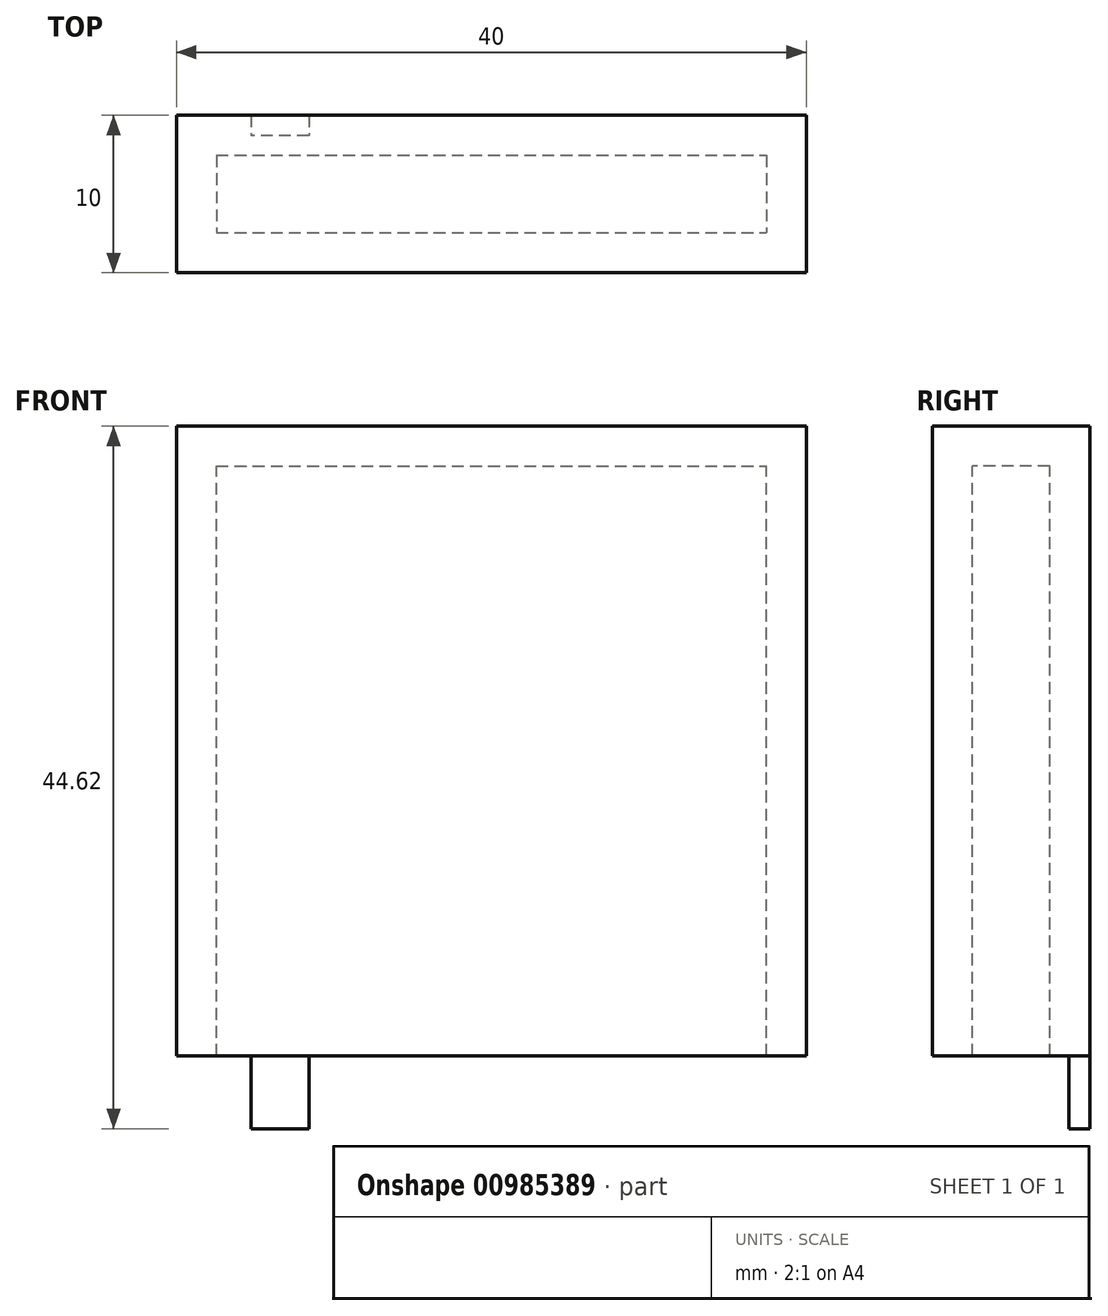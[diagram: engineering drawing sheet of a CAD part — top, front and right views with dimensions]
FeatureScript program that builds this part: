
annotation { "Feature Type Name" : "Feature", "Feature Type Description" : "" }
export const myFeature = defineFeature(function(context is Context, id is Id, definition is map)
    precondition{}
    {
        {
            var Q0;
            Q0=qCreatedBy(makeId("Front.planeOp"),FACE);
            var sketch = newSketch(context, id + "F0", { "sketchPlane" : qUnion([Q0])});
            skLineSegment(sketch, "E0.bottom", {"start": v(0, 0) * mm, "end": v(40, 0) * mm});
            skLineSegment(sketch, "E0.top", {"start": v(0, 40) * mm, "end": v(40, 40) * mm});
            skLineSegment(sketch, "E0.left", {"start": v(0, 0) * mm, "end": v(0, 40) * mm});
            skLineSegment(sketch, "E0.right", {"start": v(40, 0) * mm, "end": v(40, 40) * mm});
            skSolve(sketch);
        }
        {
            var Q0;
            Q0=makeQuery(id+"F0.imprint","IMPRINT",FACE,{"disambiguationData":[TD([[makeQuery(id+"F0.imprint","IMPRINT",EDGE,{"derivedFrom":sQuery(id+"F0.wireOp",EDGE,"E0.bottom")}),1.0]])]});
            extrude(context, id + "F1", {"entities" : qUnion([Q0]), "oppositeDirection" : true, "depth" : 10 * mm, "offsetDistance" : 25.4 * mm});
        }
        {
            var Q0;
            Q0=makeQuery(id+"F1.opExtrude","SWEPT_FACE",FACE,{"disambiguationData":[OSD([sQuery(id+"F0.wireOp",EDGE,"E0.bottom")])]});
            shell(context, id + "F2", {"entities" : qUnion([Q0]), "thickness" : 2.54 * mm});
        }
        {
            var Q0;
            Q0=makeQuery(id+"F1.opExtrude","SWEPT_FACE",FACE,{"disambiguationData":[OSD([sQuery(id+"F0.wireOp",EDGE,"E0.bottom")])]});
            var sketch = newSketch(context, id + "F3", { "sketchPlane" : qUnion([Q0])});
            skLineSegment(sketch, "E1.bottom", {"start": v(8.4, -10) * mm, "end": v(4.72, -10) * mm});
            skLineSegment(sketch, "E1.top", {"start": v(8.4, -8.7) * mm, "end": v(4.72, -8.7) * mm});
            skLineSegment(sketch, "E1.left", {"start": v(8.4, -10) * mm, "end": v(8.4, -8.7) * mm});
            skLineSegment(sketch, "E1.right", {"start": v(4.72, -10) * mm, "end": v(4.72, -8.7) * mm});
            skSolve(sketch);
        }
        {
            var Q0;
            Q0=makeQuery(id+"F3.imprint","IMPRINT",FACE,{"disambiguationData":[TD([[makeQuery(id+"F3.imprint","IMPRINT",EDGE,{"derivedFrom":sQuery(id+"F3.wireOp",EDGE,"E1.bottom")}),1.0]])]});
            extrude(context, id + "F4", {"entities" : qUnion([Q0]), "operationType" : NewBodyOperationType.ADD, "depth" : 4.62 * mm, "offsetDistance" : 25.4 * mm});
        }
    });
